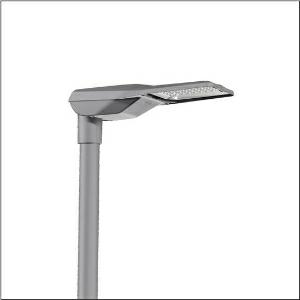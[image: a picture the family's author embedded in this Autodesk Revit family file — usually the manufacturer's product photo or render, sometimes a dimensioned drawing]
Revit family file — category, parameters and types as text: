
# Revit family: streetlight_sl_21_iq_mini___pl52_5xe2h41g08gb_5dc3
name_source: partatom
category: Lighting Fixtures
units: mm (PartAtom-declared; Revit-internal decimal feet)

## family parameters
Cut with Voids When Loaded = No
Host = Face
Light Source = No
Part Type = Normal
Room Calculation Point = No
Round Connector Dimension = Use Diameter
Shared = No

## types (1)
- --- (1 x LED, 5810 lm, 37.1 W, 4000K)
    Apparent Load = 37 VA
    CIE Flux Codes = 27 59 98 100 100
    Color Rendering = 70
    Color Temperature = 4000K
    Default Elevation = 1800 mm
    Description = Streetlight SL 21 iQ mini, mast luminaire, primary light control with lens, of PMMA, primary optical cover: cover, of toughened safety glass, transparent, light distribution: PL52, light emission: direct distribution, primary light characteristic: asymmetric, installation type: post-top, side-entry, LED, High Power LED, rated luminous flux: 5.810lm, luminous efficacy: 157lm/W, light colour: 740, colour temperature: 4000K, control gear: iQ Street-Remote, control: Street-Remote, Auto-Match, Temp-Guard, Lumen-Switch, Night-Set, Smart-Wire, Light-Fading, Desk-Remote (wireless, voltage-free reading and setting of iQ features in the workshop via application-optimized NFC function/RFID function), optimised constant luminous flux control (CLO 2.0), pre-setting: linear dimming characteristic, mains connection: 220..240V, AC, 50/60Hz, start of lifetime: 37W, end of service life: 39W, reduction: 18W, luminaire housing, of diecast aluminium, powder-coated, Siteco® metallic grey (DB 702S), corrosivity category C5 mid according to DIN EN ISO 12944, please order mast flange separately, inclination adjustable: 0°, 5°, 10°, 15°, sealing non-destructively replaceable, multi-level sealing system, length: 628mm, width: 235mm, height: 110mm, mast flange for spigot size: 42mm (side-entry): 5XC10008XM4, 60/48mm (side-entry/post-top): 5XC10108XM2, 76/60mm (side-entry/post-top): 5XC10108XM1, mounting height: 4..8m, protection rating (complete): IP66, insulation class (complete): insulation class II (safety insulation), certification: CE, ENEC, ENEC+, VDE, impact resistance: IK10, permissible operating ambient temperature for outdoor applications: -40..+50°C, standard-compliant lighting for roads and squares, packaging unit: 1 piece

Light Distribution: PL52
    Height = 110 mm
    Lamp = 1 x LED
    Lamp Light Flux = 5810 lm
    Lamp Power = 37.1 W
    Lamp count = 1
    Length = 625 mm
    Luminous efficacy = 157 lm/W
    Manufacturer = Siteco
    ModVariant = No
    Model = 5XE2H41G08GB
    Number of Poles = 1
    OnlyDefault = Yes
    Power Factor = 1
    Product Name = Streetlight SL 21 iQ mini | PL52
    Product group = mast luminaire | pylon top
    ProductGroupID = 6100
    Protection Class = Protection class II
    Protection Degree = IP 66
    RLX_Detail_Level = 1
    RLX_Emergency_Light_Flux = 0 lm
    RLX_Emergency_Type = 0
    RLX_Emergency_Type_DB = No
    RlxData = <blob elided: 35993 chars, md5=60d08f87>
    Socket = socket
    Standby Power = 0 W
    System Light Flux = 5810 lm
    System Power = 37 W
    Type Comments = factory setting: luminous flux: 100 % | dim-lin: 254 | 385 mA
    Type Image = l_1003519.jpg
    URL = http://relux.com
    VarID = @adj_190242
    Voltage = 0 V
    Weight = 0.00 kg
    Width = 234 mm

## geometry (parser evidence)
native form markers: Blend x4, Sweep x10
no freeform markers — native parametric forms only
